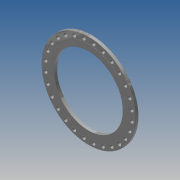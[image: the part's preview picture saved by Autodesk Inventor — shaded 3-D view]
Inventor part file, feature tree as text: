
AUTODESK INVENTOR PART (.ipt)
format: ipt  version: 2017.3 (Build 213257000, 257)  size: 261,120 bytes
history: native  units: in
note: dims shown in document units (in); Inventor stores cm internally (conversion verified against a paired STEP export)
features: chamfer x3, sketch x3, extrude x2, hole x1, pattern_circular x1
ambient origin geometry x8: Origin, YZ Plane, XZ Plane, XY Plane, X Axis, Y Axis, Z Axis, Center Point
bodies: Solid1 (feature_tree)
feature tree (10):
  extrude  "Extrusion1"  Depth=30.5in
  hole  "Hole1"  [1 undecoded]
  chamfer  "Chamfer1"  Distance=11.0236in Angle=360.0deg
  pattern_circular  "Circular Pattern1"  Angle=45.0deg  [1 undecoded]
  chamfer  "Chamfer2"  Distance=0.0625in Angle=45.0deg
  chamfer  "Chamfer4"  Distance=0.0312in Angle=45.0deg
  extrude  "Extrusion3"  Depth=0.0625in
  sketch  "Sketch1"  dims[d0=41.75in d1=30.5in]
  sketch  "Sketch2"  dims[d2=1.3125in d3=0.0in d4=38.5in]
  sketch  "Sketch4"  dims[d5=0.0442in d6=1.625in d7=0.75in d8=0.375in d9=0.25in d10=0.5635in d11=1.0in d12=0.8108in d13=11.0236in d14=360.0deg d16=0.0312in d17=0.125in d18=45.0deg d19=0.0625in d20=0.125in d21=45.0deg d28=0.0312in d29=0.125in d30=45.0deg d31=36.0in d32=0.0625in d33=0.0in]
note: 2 required parameter values undecoded (feature->parameter linkage not recoverable at this tier; creation-order binding heuristic only, values carry confidence <= 0.55)
